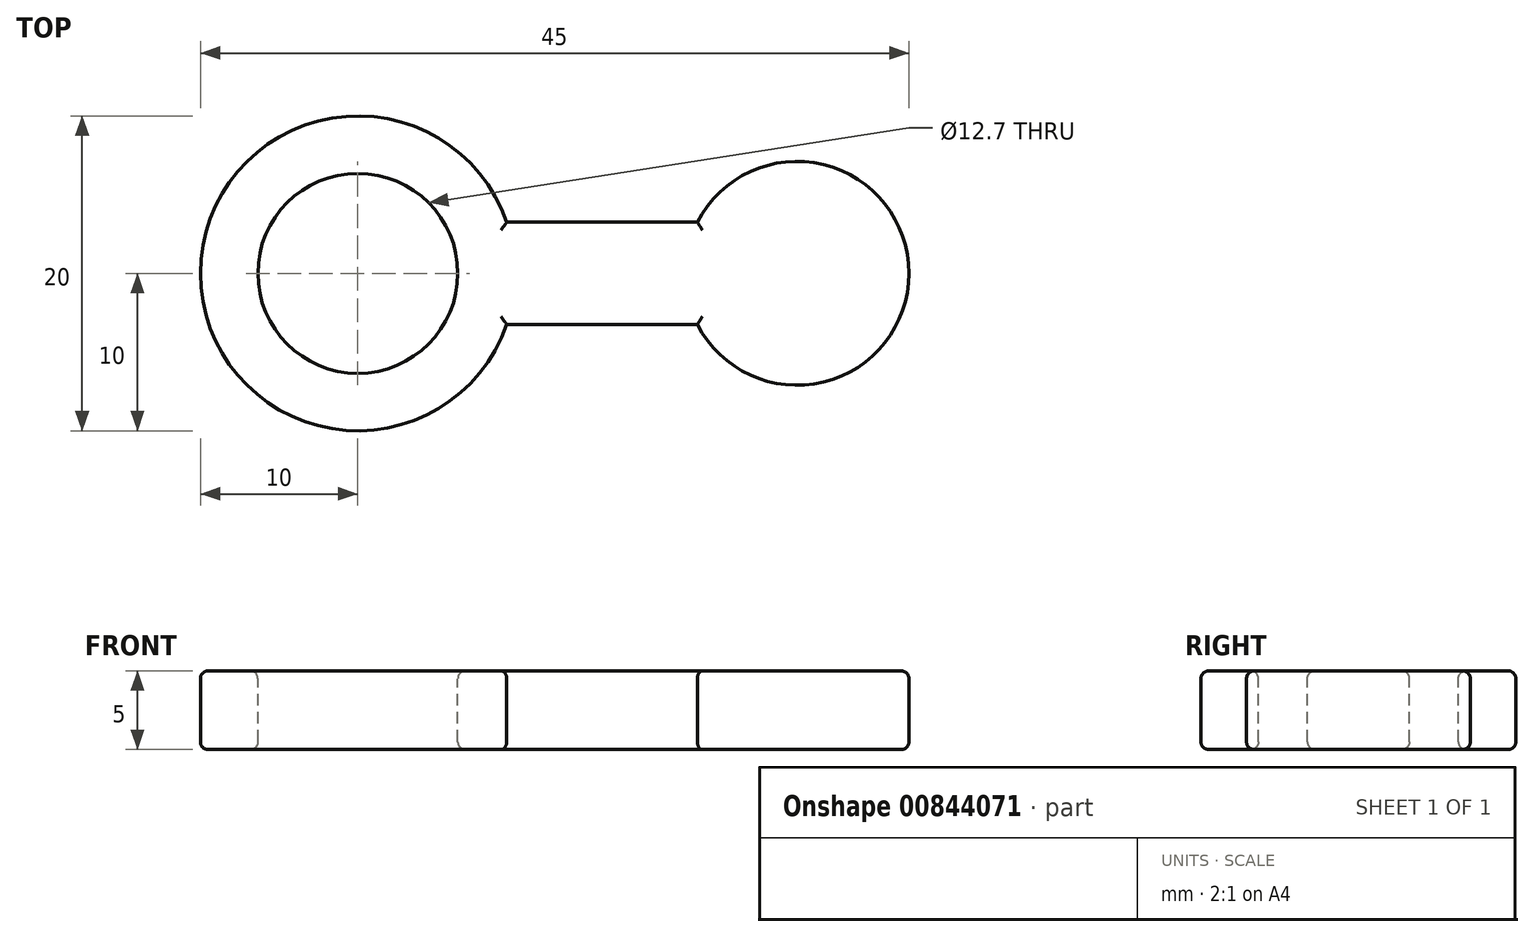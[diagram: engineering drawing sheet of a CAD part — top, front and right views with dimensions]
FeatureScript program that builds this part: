
annotation { "Feature Type Name" : "Feature", "Feature Type Description" : "" }
export const myFeature = defineFeature(function(context is Context, id is Id, definition is map)
    precondition{}
    {
        {
            var Q0;
            Q0=qCreatedBy(makeId("Top.planeOp"),FACE);
            var sketch = newSketch(context, id + "F0", { "sketchPlane" : qUnion([Q0])});
            skCircle(sketch, "E0", {"center": v(0, 0) * mm, "radius": 6.35 * mm});
            skCircle(sketch, "E1", {"center": v(0, 0) * mm, "radius": 10 * mm});
            skCircle(sketch, "E2", {"center": v(27.9, 0) * mm, "radius": 7.1 * mm});
            skLineSegment(sketch, "E3", {"start": v(9.46, 3.25) * mm, "end": v(21.57, 3.25) * mm});
            skLineSegment(sketch, "E4", {"start": v(0, 0) * mm, "end": v(35, 0) * mm, "construction": true});
            skLineSegment(sketch, "E5.MirrorCS", {"start": v(9.46, -3.25) * mm, "end": v(21.57, -3.25) * mm});
            skSolve(sketch);
        }
        {
            var Q0;
            Q0 = qSketchRegion(id + "F0", true);
            extrude(context, id + "F1", {"entities" : qUnion([Q0]), "endBound" : BoundingType.SYMMETRIC, "oppositeDirection" : true, "depth" : 5 * mm, "offsetDistance" : 25 * mm});
        }
        {
            var Q0;
            Q0=makeQuery(id+"F1.opExtrude","CAP_FACE",FACE,{"disambiguationData":[OSD([sQuery(id+"F0.wireOp",EDGE,"E0"),sQuery(id+"F0.wireOp",EDGE,"E1"),sQuery(id+"F0.wireOp",EDGE,"E2"),sQuery(id+"F0.wireOp",EDGE,"E3"),sQuery(id+"F0.wireOp",EDGE,"E5.MirrorCS")])],"isStart":true});
            var Q1;
            Q1=makeQuery(id+"F1.opExtrude","CAP_FACE",FACE,{"disambiguationData":[OSD([sQuery(id+"F0.wireOp",EDGE,"E0"),sQuery(id+"F0.wireOp",EDGE,"E1"),sQuery(id+"F0.wireOp",EDGE,"E2"),sQuery(id+"F0.wireOp",EDGE,"E3"),sQuery(id+"F0.wireOp",EDGE,"E5.MirrorCS")])],"isStart":false});
            fillet(context, id + "F2", {"entities" : qUnion([Q0, Q1]), "radius" : .5 * mm, "tangentPropagation" : true, "allowEdgeOverflow" : false});
        }
    });
